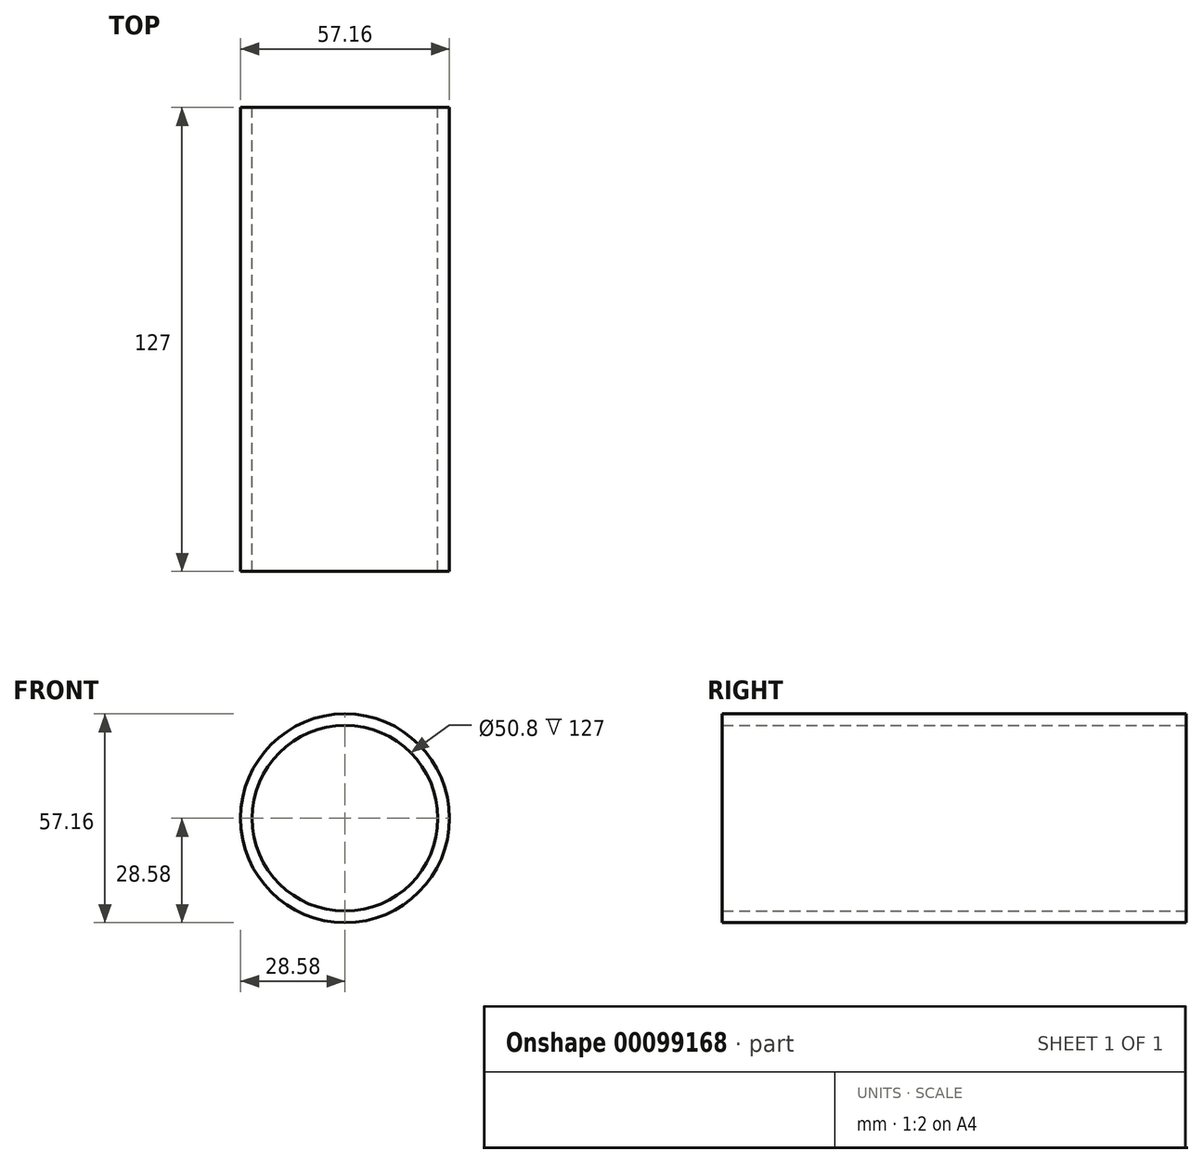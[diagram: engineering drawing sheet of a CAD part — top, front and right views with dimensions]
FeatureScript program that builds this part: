
annotation { "Feature Type Name" : "Feature", "Feature Type Description" : "" }
export const myFeature = defineFeature(function(context is Context, id is Id, definition is map)
    precondition{}
    {
        {
            var Q0;
            Q0=qCreatedBy(makeId("Front.planeOp"),FACE);
            var sketch = newSketch(context, id + "F0", { "sketchPlane" : qUnion([Q0])});
            skCircle(sketch, "E0", {"center": v(0, 0) * mm, "radius": 28.58 * mm});
            skCircle(sketch, "E1", {"center": v(0, 0) * mm, "radius": 25.4 * mm});
            skSolve(sketch);
        }
        {
            var Q0;
            Q0 = qSketchRegion(id + "F0", true);
            extrude(context, id + "F1", {"entities" : qUnion([Q0]), "endBound" : BoundingType.SYMMETRIC, "depth" : 127 * mm});
        }
    });
